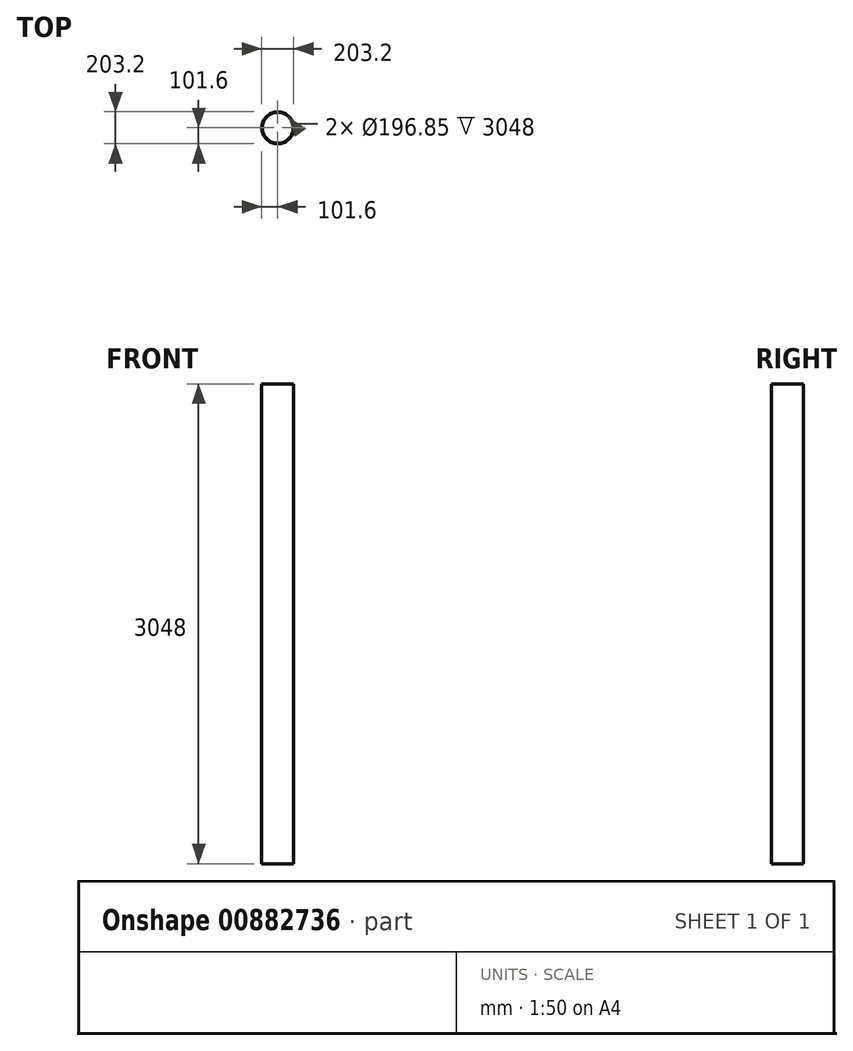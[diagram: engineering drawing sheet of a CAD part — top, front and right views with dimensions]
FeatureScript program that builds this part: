
annotation { "Feature Type Name" : "Feature", "Feature Type Description" : "" }
export const myFeature = defineFeature(function(context is Context, id is Id, definition is map)
    precondition{}
    {
        {
            var Q0;
            Q0=qCreatedBy(makeId("Top.planeOp"),FACE);
            var sketch = newSketch(context, id + "F0", { "sketchPlane" : qUnion([Q0])});
            skCircle(sketch, "E0", {"center": v(0, 0) * mm, "radius": 101.6 * mm});
            skCircle(sketch, "E1", {"center": v(0, 0) * mm, "radius": 98.43 * mm});
            skSolve(sketch);
        }
        {
            var Q0;
            Q0=makeQuery(id+"F0.imprint","IMPRINT",FACE,{"disambiguationData":[TD([[makeQuery(id+"F0.imprint","IMPRINT",EDGE,{"derivedFrom":sQuery(id+"F0.wireOp",EDGE,"E0")}),1.0]])]});
            extrude(context, id + "F1", {"entities" : qUnion([Q0]), "depth" : 3048 * mm, "offsetDistance" : 25.4 * mm});
        }
    });
